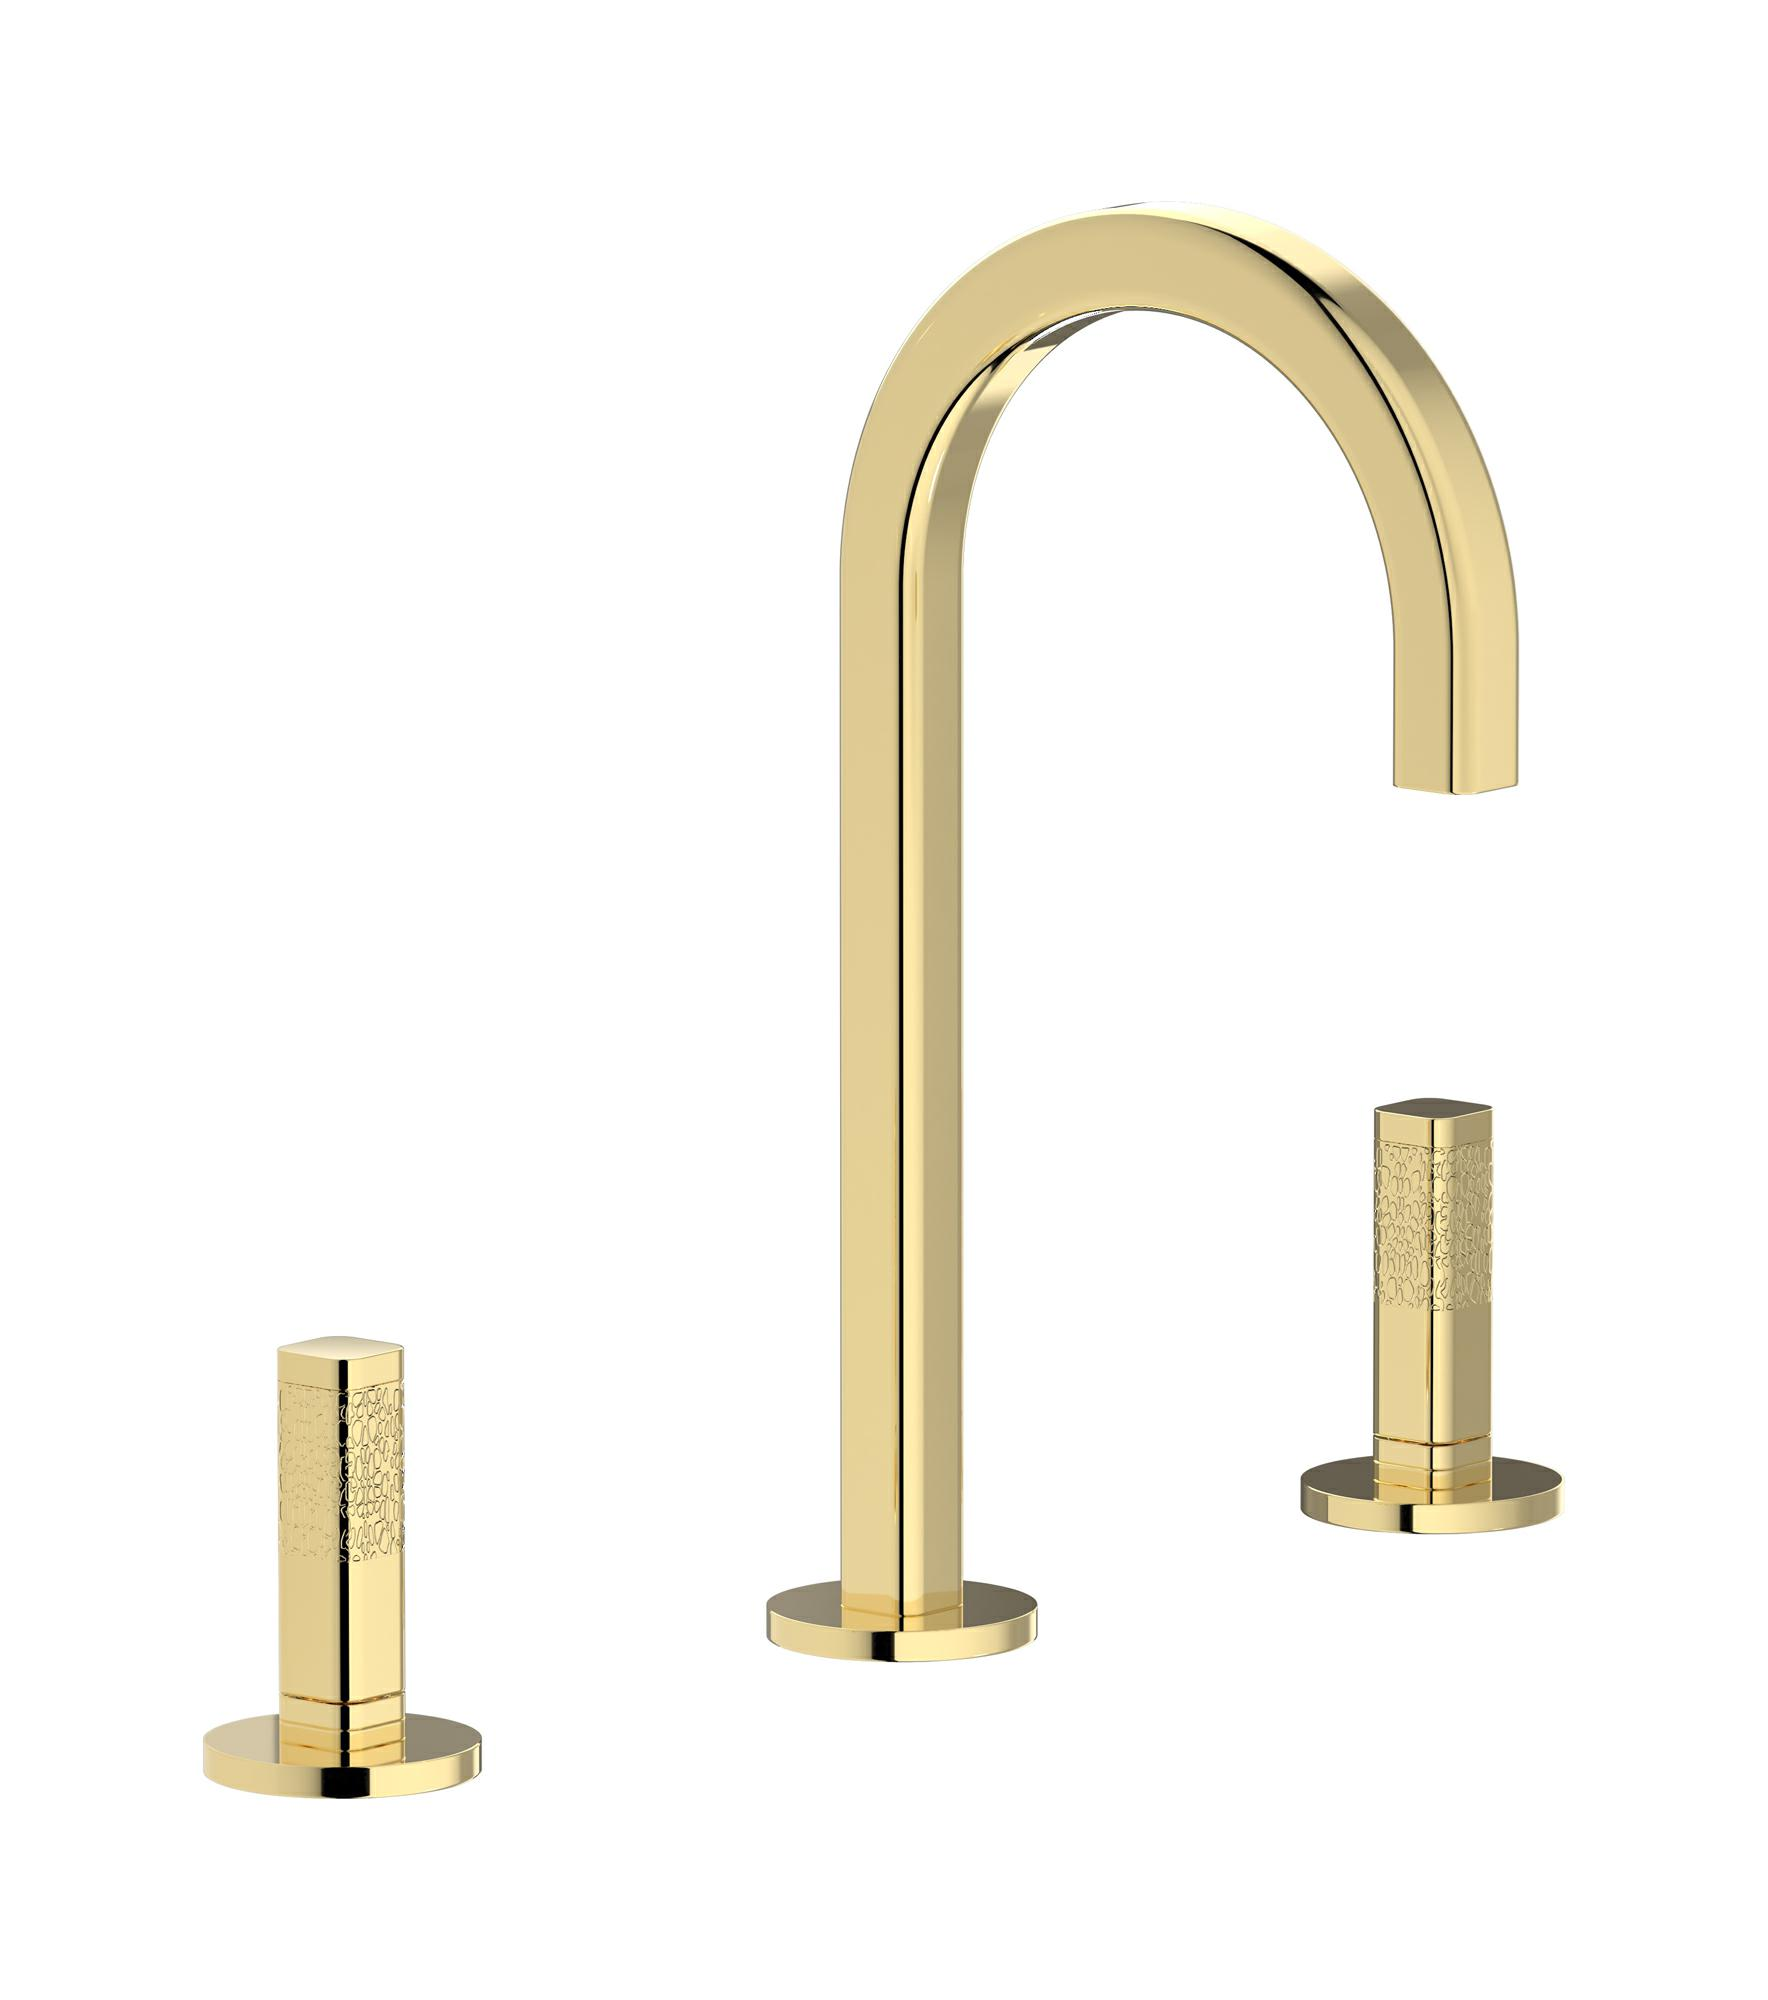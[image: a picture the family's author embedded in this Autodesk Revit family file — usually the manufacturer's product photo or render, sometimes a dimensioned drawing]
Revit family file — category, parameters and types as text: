
# Revit family: EI392_4
name_source: partatom
category: Apparecchi idraulici
units: mm (PartAtom-declared; Revit-internal decimal feet)

## family parameters
Basato su piano di lavoro = No
Condiviso = No
Mantieni orientamento annotazione = No
Numero OmniClass = 23.45.55.17
Punto di calcolo locali = No
Quota connettore circolare = Usa diametro
Sempre verticale = Sì
Taglio con vuoti quando caricato = No
Tipo di parte = Normale
Titolo OmniClass = Mixing Faucets

## types (12) — shared parameters
Cold water inlet = 10 mm  [stored 0.0328084 ft]
Commenti sul tipo = Washbasin
Connessione CW = No
Connessione HW = No
Connessione di scarico = No
Connessione di ventilazione = No
Descrizione = Three hole washbasin complete
Hot water inlet = 10 mm  [stored 0.0328084 ft]
Produttore = IB Rubinetterie S.p.A.
URL = https://www.weareib.it
zero-valued in all types: Prospetto di default

## per-type parameters (varying)
| type | Finishes surface | Immagine tipo | Modello |
| Chrome | IB_Chrome | EI392CC_4.jpg | EI392CC_4 |
| Brushed nickel | IB_Brushed nickel | EI392SS_4.jpg | EI392SS_4 |
| Natural brass | IB_Brass | EI392ON_4.jpg | EI392ON_4 |
| Matt black | IB_matt black | EI392NP_4.jpg | EI392NP_4 |
| Black chrome | IB_Black chrome | EI392CF_4.jpg | EI392CF_4 |
| Brushed black chrome | IB_Brushed black chrome | EI392CS_4.jpg | EI392CS_4 |
| Pale gold | IB_Pale gold | EI392II_4.jpg | EI392II_4 |
| Brushed pale gold | IB_brushed pale gold | EI392IS_4.jpg | EI392IS_4 |
| Rose gold | IB_Rose gold | EI392RS_4.jpg | EI392RS_4 |
| Brushed rose gold | IB_Brushed rose gold | EI392SR_4.jpg | EI392SR_4 |
| Gold | IB_gold | EI392OO_4.jpg | EI392OO_4 |
| Brushed gold | IB_brushed gold | EI392OS_4.jpg | EI392OS_4 |

note: [stored X ft] marks values corroborated as IEEE doubles in the binary element streams (Revit-internal decimal feet)
